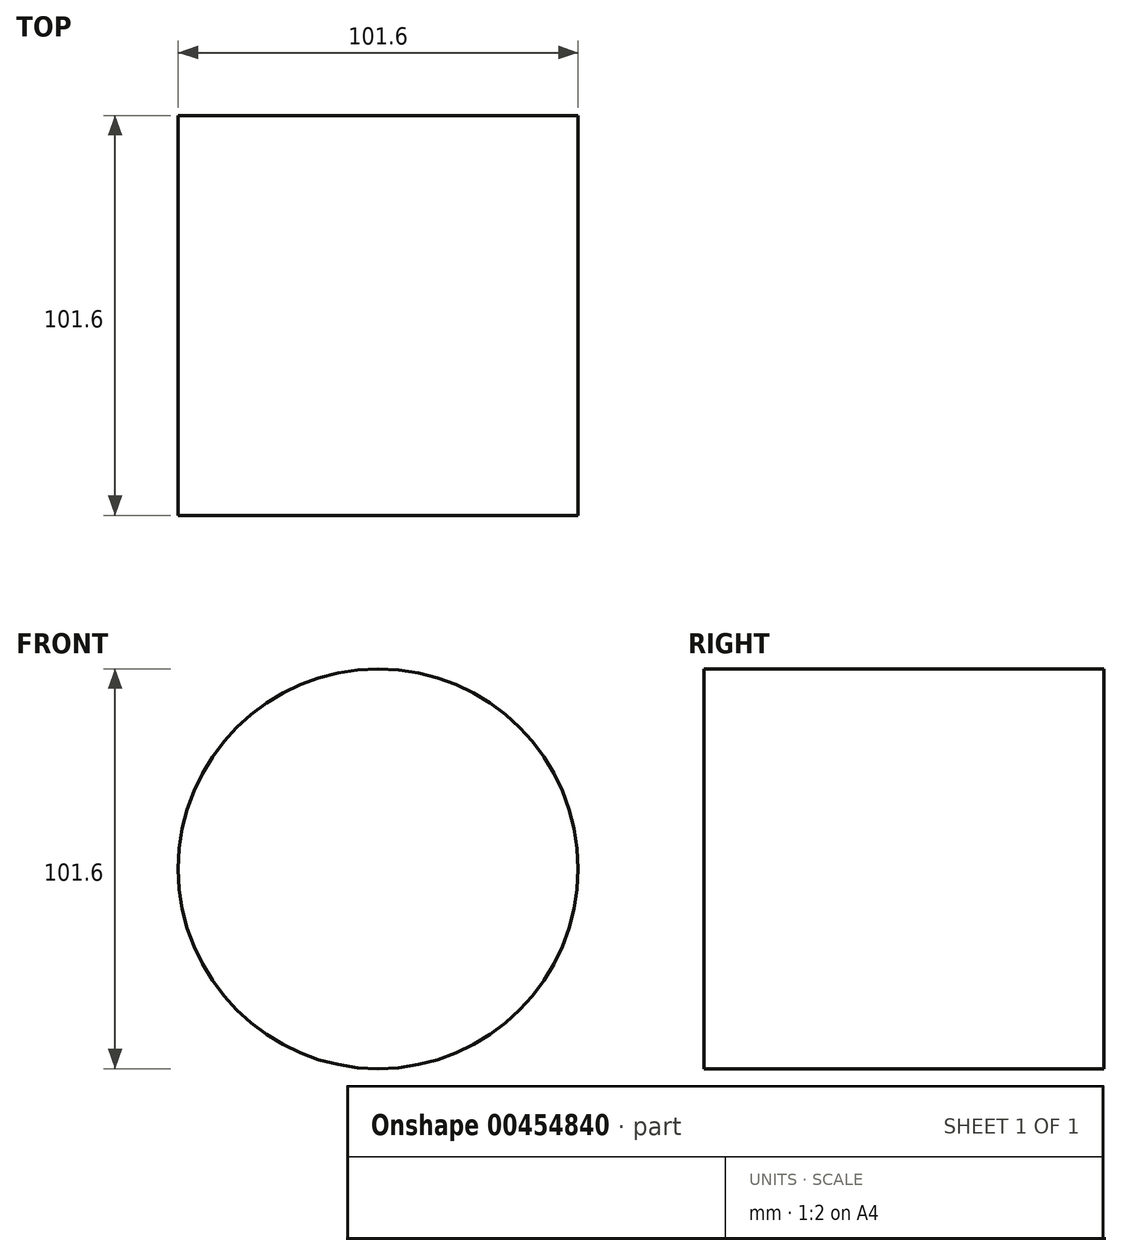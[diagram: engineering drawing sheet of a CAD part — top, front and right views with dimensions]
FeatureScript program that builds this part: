
annotation { "Feature Type Name" : "Feature", "Feature Type Description" : "" }
export const myFeature = defineFeature(function(context is Context, id is Id, definition is map)
    precondition{}
    {
        {
            var Q0;
            Q0=qCreatedBy(makeId("Front.planeOp"),FACE);
            var sketch = newSketch(context, id + "F0", { "sketchPlane" : qUnion([Q0])});
            skCircle(sketch, "E0", {"center": v(0, 0) * mm, "radius": 50.8 * mm});
            skSolve(sketch);
        }
        {
            var Q0;
            Q0 = qSketchRegion(id + "F0", true);
            extrude(context, id + "F1", {"entities" : qUnion([Q0]), "endBound" : BoundingType.SYMMETRIC, "depth" : 101.6 * mm, "offsetDistance" : 25.4 * mm});
        }
    });
